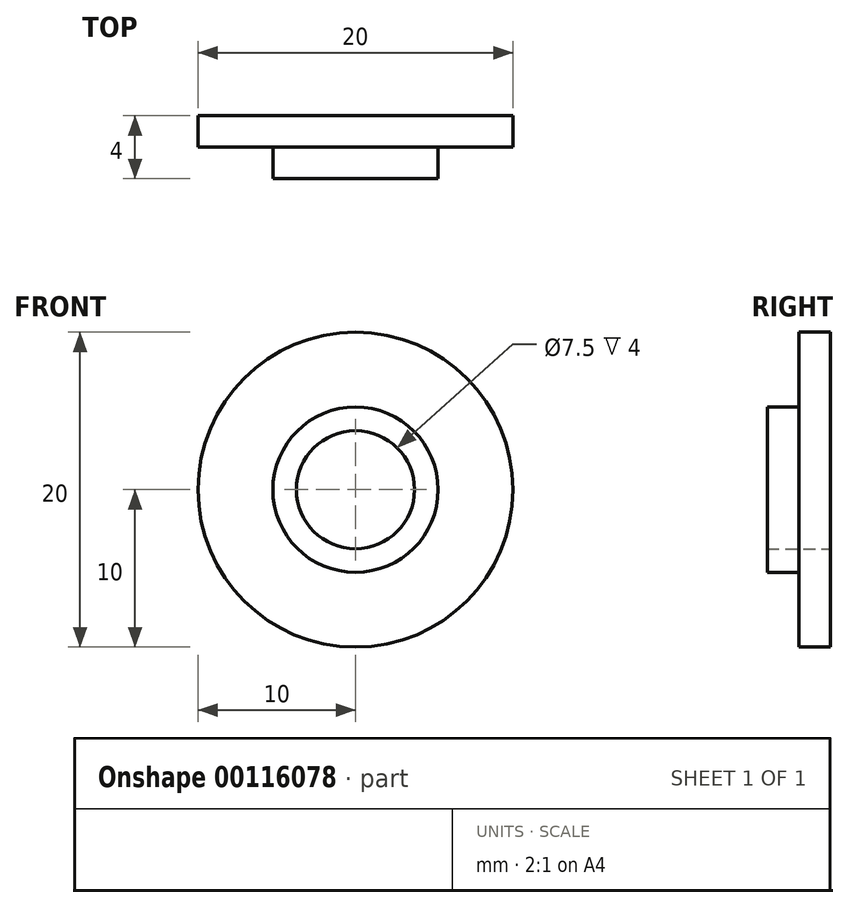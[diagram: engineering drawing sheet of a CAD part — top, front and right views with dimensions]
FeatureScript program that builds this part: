
annotation { "Feature Type Name" : "Feature", "Feature Type Description" : "" }
export const myFeature = defineFeature(function(context is Context, id is Id, definition is map)
    precondition{}
    {
        {
            var Q0;
            Q0=qCreatedBy(makeId("Front.planeOp"),FACE);
            var sketch = newSketch(context, id + "F0", { "sketchPlane" : qUnion([Q0])});
            skCircle(sketch, "E0", {"center": v(0, 0) * mm, "radius": 3.75 * mm});
            skCircle(sketch, "E1", {"center": v(0, 0) * mm, "radius": 5.25 * mm});
            skCircle(sketch, "E2", {"center": v(0, 0) * mm, "radius": 10 * mm});
            skSolve(sketch);
        }
        {
            var Q0;
            Q0=makeQuery(id+"F0.imprint","IMPRINT",FACE,{"disambiguationData":[TD([[makeQuery(id+"F0.imprint","IMPRINT",EDGE,{"derivedFrom":sQuery(id+"F0.wireOp",EDGE,"E1")}),-1.0]])]});
            var Q1;
            Q1=makeQuery(id+"F0.imprint","IMPRINT",FACE,{"disambiguationData":[TD([[makeQuery(id+"F0.imprint","IMPRINT",EDGE,{"derivedFrom":sQuery(id+"F0.wireOp",EDGE,"E0")}),-1.0]])]});
            extrude(context, id + "F1", {"entities" : qUnion([Q0, Q1]), "depth" : 2 * mm, "offsetDistance" : 25 * mm});
        }
        {
            var Q0;
            Q0=makeQuery(id+"F0.imprint","IMPRINT",FACE,{"disambiguationData":[TD([[makeQuery(id+"F0.imprint","IMPRINT",EDGE,{"derivedFrom":sQuery(id+"F0.wireOp",EDGE,"E0")}),-1.0]])]});
            extrude(context, id + "F2", {"entities" : qUnion([Q0]), "operationType" : NewBodyOperationType.ADD, "depth" : 4 * mm, "offsetDistance" : 25 * mm});
        }
    });
